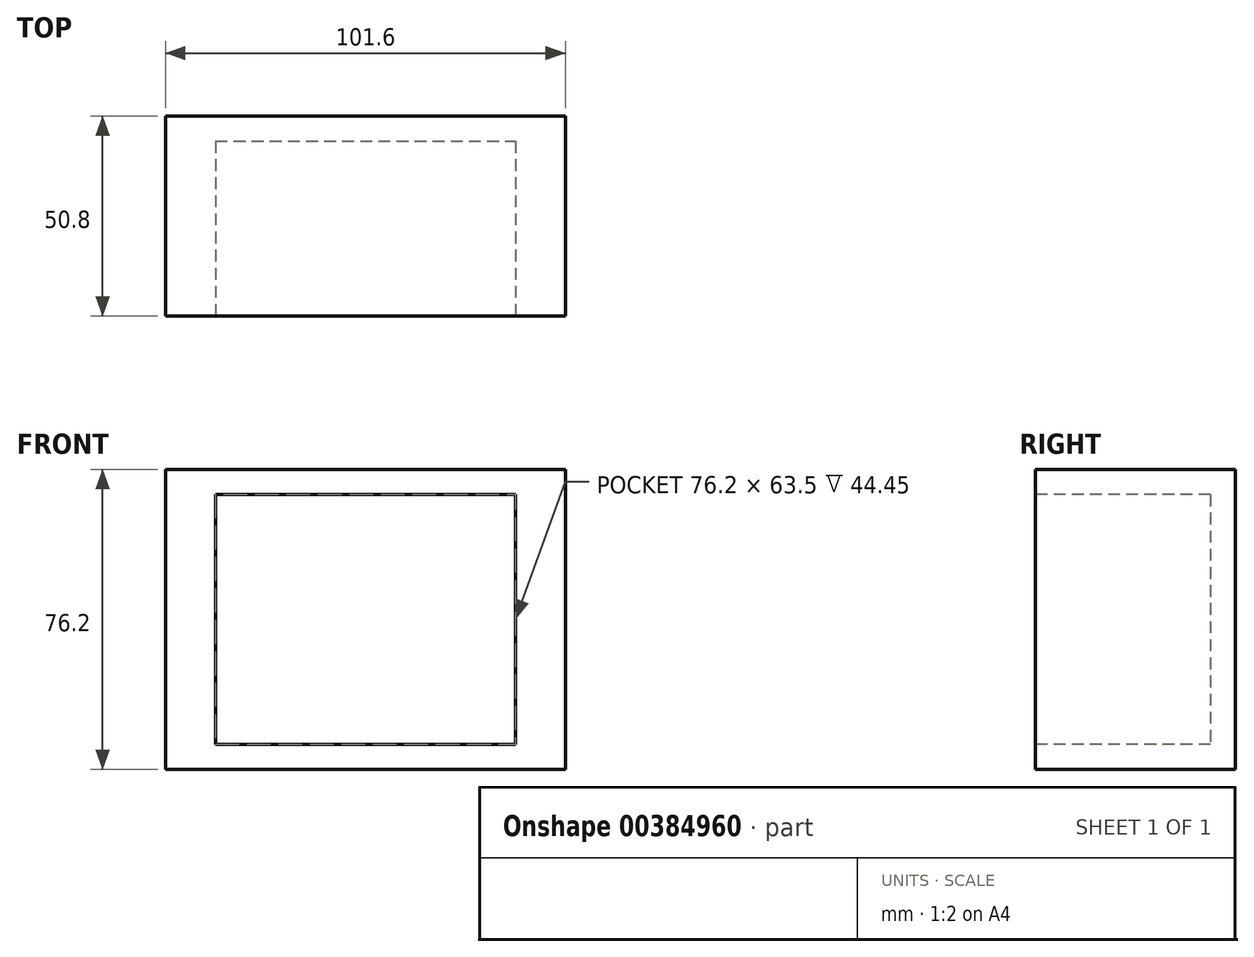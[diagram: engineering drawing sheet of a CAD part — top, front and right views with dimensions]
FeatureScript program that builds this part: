
annotation { "Feature Type Name" : "Feature", "Feature Type Description" : "" }
export const myFeature = defineFeature(function(context is Context, id is Id, definition is map)
    precondition{}
    {
        {
            var Q0;
            Q0=qCreatedBy(makeId("Front.planeOp"),FACE);
            var sketch = newSketch(context, id + "F0", { "sketchPlane" : qUnion([Q0])});
            skLineSegment(sketch, "E0.bottom", {"start": v(-50.8, 38.1) * mm, "end": v(50.8, 38.1) * mm});
            skLineSegment(sketch, "E0.top", {"start": v(-50.8, -38.1) * mm, "end": v(50.8, -38.1) * mm});
            skLineSegment(sketch, "E0.left", {"start": v(-50.8, 38.1) * mm, "end": v(-50.8, -38.1) * mm});
            skLineSegment(sketch, "E0.right", {"start": v(50.8, 38.1) * mm, "end": v(50.8, -38.1) * mm});
            skPoint(sketch, "E0.middle", {"position": v(0, 0) * mm});
            skSolve(sketch);
        }
        {
            var Q0;
            Q0=makeQuery(id+"F0.imprint","IMPRINT",FACE,{"disambiguationData":[TD([[makeQuery(id+"F0.imprint","IMPRINT",EDGE,{"derivedFrom":sQuery(id+"F0.wireOp",EDGE,"E0.bottom")}),-1.0]])]});
            extrude(context, id + "F1", {"entities" : qUnion([Q0]), "flatOperationType" : FlatOperationType.REMOVE, "offsetDistance" : 25.4 * mm, "depth" : 50.8 * mm, "domain" : OperationDomain.MODEL});
        }
        {
            var Q0;
            Q0=makeQuery(id+"F1.opExtrude","CAP_FACE",FACE,{"disambiguationData":[OSD([sQuery(id+"F0.wireOp",EDGE,"E0.bottom"),sQuery(id+"F0.wireOp",EDGE,"E0.top"),sQuery(id+"F0.wireOp",EDGE,"E0.left"),sQuery(id+"F0.wireOp",EDGE,"E0.right")])],"isStart":false});
            var sketch = newSketch(context, id + "F2", { "sketchPlane" : qUnion([Q0])});
            skLineSegment(sketch, "E1.bottom", {"start": v(-38.1, 31.75) * mm, "end": v(38.1, 31.75) * mm});
            skLineSegment(sketch, "E1.top", {"start": v(-38.1, -31.75) * mm, "end": v(38.1, -31.75) * mm});
            skLineSegment(sketch, "E1.left", {"start": v(-38.1, 31.75) * mm, "end": v(-38.1, -31.75) * mm});
            skLineSegment(sketch, "E1.right", {"start": v(38.1, 31.75) * mm, "end": v(38.1, -31.75) * mm});
            skPoint(sketch, "E1.middle", {"position": v(0, 0) * mm});
            skSolve(sketch);
        }
        {
            var Q0;
            Q0=makeQuery(id+"F2.imprint","IMPRINT",FACE,{"disambiguationData":[TD([[makeQuery(id+"F2.imprint","IMPRINT",EDGE,{"derivedFrom":sQuery(id+"F2.wireOp",EDGE,"E1.bottom")}),-1.0]])]});
            extrude(context, id + "F3", {"entities" : qUnion([Q0]), "operationType" : NewBodyOperationType.REMOVE, "oppositeDirection" : true, "depth" : 44.45 * mm});
        }
    });
